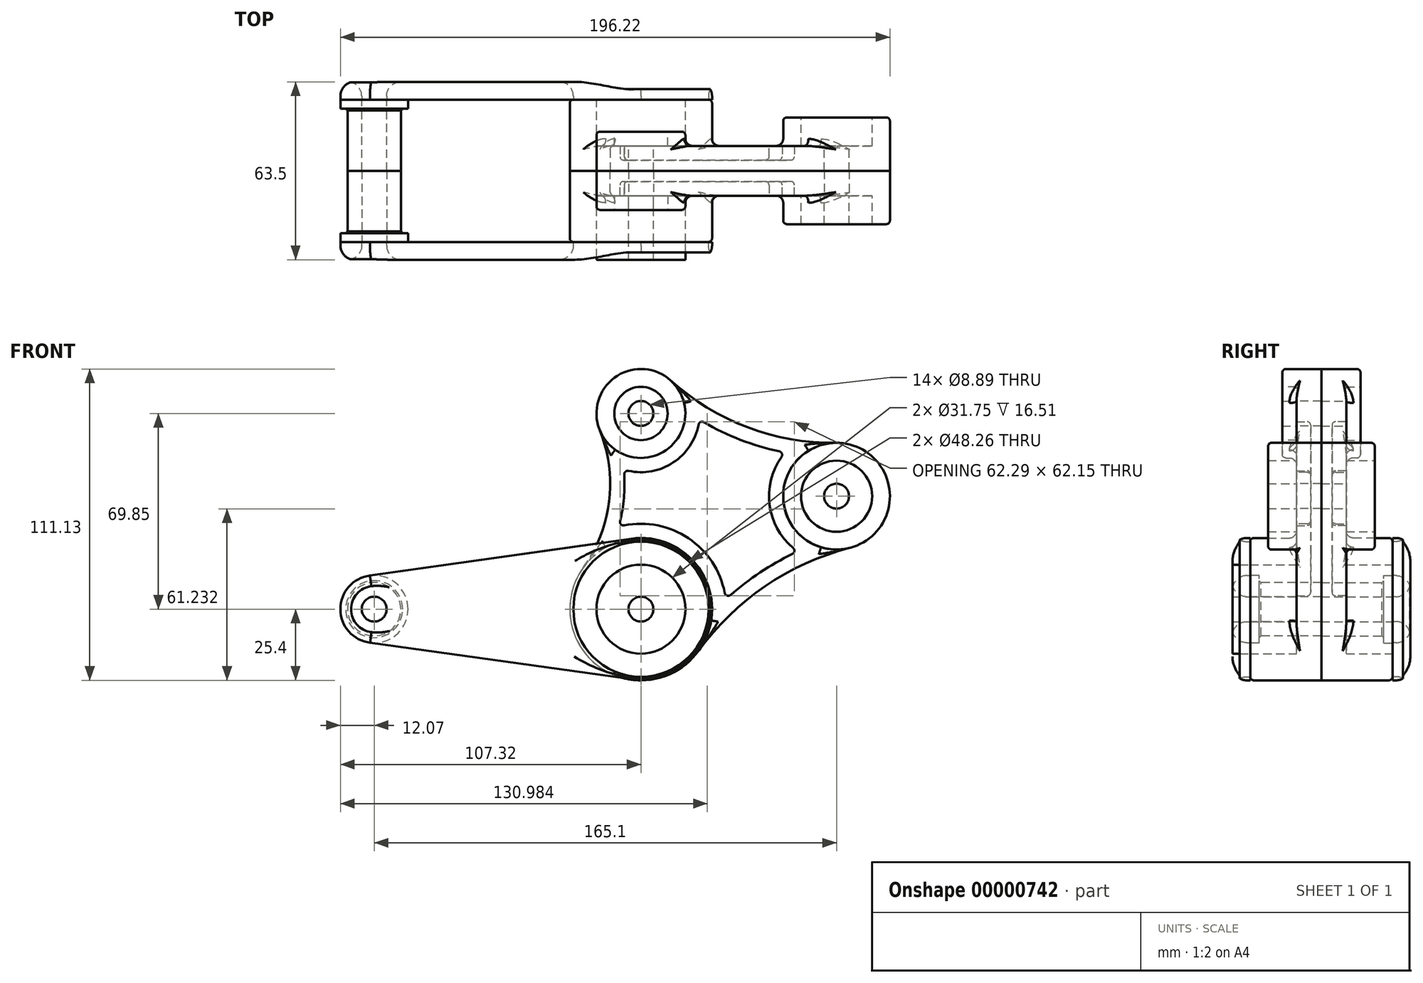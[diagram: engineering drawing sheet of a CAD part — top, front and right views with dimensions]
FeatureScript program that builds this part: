
annotation { "Feature Type Name" : "Feature", "Feature Type Description" : "" }
export const myFeature = defineFeature(function(context is Context, id is Id, definition is map)
    precondition{}
    {
        {
            var Q0;
            Q0=qCreatedBy(makeId("Front.planeOp"),FACE);
            var sketch = newSketch(context, id + "F0", { "sketchPlane" : qUnion([Q0])});
            skCircle(sketch, "E0", {"center": v(0, 0) * mm, "radius": 25.4 * mm});
            skCircle(sketch, "E1", {"center": v(0, 69.85) * mm, "radius": 15.88 * mm});
            skCircle(sketch, "E2", {"center": v(69.85, 40.33) * mm, "radius": 19.05 * mm});
            skLineSegment(sketch, "E3", {"start": v(0, 0) * mm, "end": v(69.85, 40.33) * mm, "construction": true});
            skLineSegment(sketch, "E4", {"start": v(0, 0) * mm, "end": v(74.27, 0) * mm, "construction": true});
            skArc(sketch, "E5", {"start": v(-20.58, 14.89) * mm, "mid": v(-11.3, 38.61) * mm, "end": v(-14.7, 63.85) * mm});
            skArc(sketch, "E6", {"start": v(74.6, 21.88) * mm, "mid": v(44.37, 8.2) * mm, "end": v(20.56, -14.91) * mm});
            skArc(sketch, "E7", {"start": v(10.64, 81.63) * mm, "mid": v(38.02, 64.93) * mm, "end": v(69.6, 59.38) * mm});
            skSolve(sketch);
        }
        {
            var Q0;
            {var subQ0=sQuery(id+"F0.wireOp",EDGE,"E0");var subQ1=sQuery(id+"F0.wireOp",EDGE,"E6");var subQ3=sQuery(id+"F0.wireOp",EDGE,"E5");var subQ4=makeQuery(id+"F0.imprint","INTERSECT",VERTEX,{"derivedFrom":[subQ0,subQ3]});var subQ6=sQuery(id+"F0.wireOp",EDGE,"E1");var subQ9=makeQuery(id+"F0.imprint","INTERSECT",VERTEX,{"derivedFrom":[subQ6,subQ3]});var subQ11=sQuery(id+"F0.wireOp",EDGE,"E2");var subQ13=makeQuery(id+"F0.imprint","INTERSECT",VERTEX,{"derivedFrom":[subQ11,subQ1]});var subQ14=makeQuery(id+"F0.imprint","IMPRINT",EDGE,{"disambiguationData":[TD([[subQ13,1.0]])],"derivedFrom":subQ11});Q0=qUnion([makeQuery(id+"F0.imprint","IMPRINT",FACE,{"disambiguationData":[TD([[makeQuery(id+"F0.imprint","IMPRINT",EDGE,{"disambiguationData":[TD([[subQ4,-1.0]])],"derivedFrom":subQ0}),1.0]])]}),makeQuery(id+"F0.imprint","IMPRINT",FACE,{"disambiguationData":[TD([[makeQuery(id+"F0.imprint","IMPRINT",EDGE,{"disambiguationData":[TD([[subQ9,1.0]])],"derivedFrom":subQ6}),1.0]])]}),makeQuery(id+"F0.imprint","IMPRINT",FACE,{"disambiguationData":[TD([[subQ14,1.0]])]}),makeQuery(id+"F0.imprint","IMPRINT",FACE,{"disambiguationData":[TD([[makeQuery(id+"F0.imprint","IMPRINT",EDGE,{"derivedFrom":subQ3}),-1.0]])]})]);}
            extrude(context, id + "F1", {"entities" : qUnion([Q0]), "depth" : 8.9 * mm});
        }
        {
            var Q0;
            {var subQ0=sQuery(id+"F0.wireOp",EDGE,"E1");var subQ2=makeQuery(id+"F0.imprint","INTERSECT",VERTEX,{"derivedFrom":[subQ0,sQuery(id+"F0.wireOp",EDGE,"E5")]});Q0=makeQuery(id+"F0.imprint","IMPRINT",FACE,{"disambiguationData":[TD([[makeQuery(id+"F0.imprint","IMPRINT",EDGE,{"disambiguationData":[TD([[subQ2,1.0]])],"derivedFrom":subQ0}),1.0]])]});}
            extrude(context, id + "F2", {"entities" : qUnion([Q0]), "operationType" : NewBodyOperationType.ADD, "depth" : 13.97 * mm});
        }
        {
            var Q0;
            {var subQ0=sQuery(id+"F0.wireOp",EDGE,"E2");var subQ2=makeQuery(id+"F0.imprint","INTERSECT",VERTEX,{"derivedFrom":[subQ0,sQuery(id+"F0.wireOp",EDGE,"E6")]});Q0=makeQuery(id+"F0.imprint","IMPRINT",FACE,{"disambiguationData":[TD([[makeQuery(id+"F0.imprint","IMPRINT",EDGE,{"disambiguationData":[TD([[subQ2,1.0]])],"derivedFrom":subQ0}),1.0]])]});}
            extrude(context, id + "F3", {"entities" : qUnion([Q0]), "operationType" : NewBodyOperationType.ADD, "depth" : 19.05 * mm});
        }
        {
            var Q0;
            {var subQ0=sQuery(id+"F0.wireOp",EDGE,"E0");var subQ2=makeQuery(id+"F0.imprint","INTERSECT",VERTEX,{"derivedFrom":[subQ0,sQuery(id+"F0.wireOp",EDGE,"E5")]});Q0=makeQuery(id+"F0.imprint","IMPRINT",FACE,{"disambiguationData":[TD([[makeQuery(id+"F0.imprint","IMPRINT",EDGE,{"disambiguationData":[TD([[subQ2,-1.0]])],"derivedFrom":subQ0}),1.0]])]});}
            extrude(context, id + "F4", {"entities" : qUnion([Q0]), "operationType" : NewBodyOperationType.ADD, "depth" : 25.4 * mm});
        }
        {
            var Q0;
            Q0=makeQuery(id+"F1.opExtrude","CAP_FACE",FACE,{"disambiguationData":[OSD([sQuery(id+"F0.wireOp",EDGE,"E0"),sQuery(id+"F0.wireOp",EDGE,"E1"),sQuery(id+"F0.wireOp",EDGE,"E2"),sQuery(id+"F0.wireOp",EDGE,"E5"),sQuery(id+"F0.wireOp",EDGE,"E6"),sQuery(id+"F0.wireOp",EDGE,"E7")])],"isStart":false});
            var sketch = newSketch(context, id + "F5", { "sketchPlane" : qUnion([Q0])});
            skCircle(sketch, "E8.0", {"center": v(0, 69.85) * mm, "radius": 20.96 * mm});
            skCircle(sketch, "E9.0", {"center": v(69.85, 40.33) * mm, "radius": 24.13 * mm});
            skCircle(sketch, "E10.0", {"center": v(0, 0) * mm, "radius": 30.48 * mm});
            skArc(sketch, "E11.0", {"start": v(-16.46, 11.91) * mm, "mid": v(-6.25, 38) * mm, "end": v(-10, 65.77) * mm});
            skArc(sketch, "E12.0", {"start": v(7.23, 77.86) * mm, "mid": v(36.23, 60.18) * mm, "end": v(69.67, 54.3) * mm});
            skArc(sketch, "E13.0", {"start": v(73.34, 26.8) * mm, "mid": v(41.51, 12.4) * mm, "end": v(16.45, -11.93) * mm});
            skSolve(sketch);
        }
        {
            var Q0;
            {var subQ5=sQuery(id+"F5.wireOp",EDGE,"E12.0");var subQ7=sQuery(id+"F5.wireOp",EDGE,"E8.0");var subQ8=makeQuery(id+"F5.imprint","INTERSECT",VERTEX,{"derivedFrom":[subQ7,subQ5]});Q0=makeQuery(id+"F5.imprint","IMPRINT",FACE,{"disambiguationData":[TD([[makeQuery(id+"F5.imprint","IMPRINT",EDGE,{"disambiguationData":[TD([[subQ8,1.0]])],"derivedFrom":subQ7}),-1.0]])]});}
            extrude(context, id + "F6", {"entities" : qUnion([Q0]), "operationType" : NewBodyOperationType.REMOVE, "oppositeDirection" : true, "depth" : 5.08 * mm});
        }
        {
            var Q0;
            Q0=makeQuery(id+"F4.opExtrude","CAP_FACE",FACE,{"disambiguationData":[OSD([sQuery(id+"F0.wireOp",EDGE,"E0")])],"isStart":false});
            var sketch = newSketch(context, id + "F7", { "sketchPlane" : qUnion([Q0])});
            skCircle(sketch, "E14", {"center": v(0, 0) * mm, "radius": 15.88 * mm});
            skCircle(sketch, "E15.0", {"center": v(0, 69.85) * mm, "radius": 15.88 * mm, "construction": true});
            skCircle(sketch, "E15.1", {"center": v(69.85, 40.33) * mm, "radius": 19.05 * mm, "construction": true});
            skCircle(sketch, "E16", {"center": v(0, 69.85) * mm, "radius": 9.53 * mm});
            skCircle(sketch, "E17", {"center": v(69.85, 40.33) * mm, "radius": 12.7 * mm});
            skSolve(sketch);
        }
        {
            var Q0;
            Q0=makeQuery(id+"F7.imprint","IMPRINT",FACE,{"disambiguationData":[TD([[makeQuery(id+"F7.imprint","IMPRINT",EDGE,{"derivedFrom":sQuery(id+"F7.wireOp",EDGE,"E14")}),1.0]])]});
            var Q1;
            Q1=makeQuery(id+"F7.imprint","IMPRINT",FACE,{"disambiguationData":[TD([[makeQuery(id+"F7.imprint","IMPRINT",EDGE,{"derivedFrom":sQuery(id+"F7.wireOp",EDGE,"E16")}),1.0]])]});
            var Q2;
            Q2=makeQuery(id+"F7.imprint","IMPRINT",FACE,{"disambiguationData":[TD([[makeQuery(id+"F7.imprint","IMPRINT",EDGE,{"derivedFrom":sQuery(id+"F7.wireOp",EDGE,"E17")}),1.0]])]});
            var Q3;
            Q3=makeQuery(id+"F1.opExtrude","CAP_FACE",FACE,{"disambiguationData":[OSD([sQuery(id+"F0.wireOp",EDGE,"E0"),sQuery(id+"F0.wireOp",EDGE,"E1"),sQuery(id+"F0.wireOp",EDGE,"E2"),sQuery(id+"F0.wireOp",EDGE,"E5"),sQuery(id+"F0.wireOp",EDGE,"E6"),sQuery(id+"F0.wireOp",EDGE,"E7")])],"isStart":false});
            extrude(context, id + "F8", {"entities" : qUnion([Q0, Q1, Q2]), "operationType" : NewBodyOperationType.REMOVE, "endBound" : BoundingType.UP_TO_SURFACE, "oppositeDirection" : true, "endBoundEntityFace" : qUnion([Q3]), "depth" : 25.4 * mm});
        }
        {
            var Q0;
            Q0=makeQuery(id+"F8.boolean.opBoolean","COPY",FACE,{"derivedFrom":makeQuery(id+"F8.opExtrude","CAP_FACE",FACE,{"disambiguationData":[OSD([sQuery(id+"F7.wireOp",EDGE,"E17")])],"isStart":false})});
            var sketch = newSketch(context, id + "F9", { "sketchPlane" : qUnion([Q0])});
            skCircle(sketch, "E18.0", {"center": v(0, 69.85) * mm, "radius": 9.53 * mm});
            skCircle(sketch, "E18.1", {"center": v(0, 0) * mm, "radius": 15.88 * mm});
            skCircle(sketch, "E18.2", {"center": v(69.85, 40.33) * mm, "radius": 12.7 * mm});
            skCircle(sketch, "E19", {"center": v(0, 0) * mm, "radius": 4.45 * mm});
            skCircle(sketch, "E20", {"center": v(0, 69.85) * mm, "radius": 4.45 * mm});
            skCircle(sketch, "E21", {"center": v(69.85, 40.33) * mm, "radius": 4.45 * mm});
            skSolve(sketch);
        }
        {
            var Q0;
            Q0=makeQuery(id+"F9.imprint","IMPRINT",FACE,{"disambiguationData":[TD([[makeQuery(id+"F9.imprint","IMPRINT",EDGE,{"derivedFrom":sQuery(id+"F9.wireOp",EDGE,"E20")}),1.0]])]});
            var Q1;
            Q1=makeQuery(id+"F9.imprint","IMPRINT",FACE,{"disambiguationData":[TD([[makeQuery(id+"F9.imprint","IMPRINT",EDGE,{"derivedFrom":sQuery(id+"F9.wireOp",EDGE,"E21")}),1.0]])]});
            var Q2;
            Q2=makeQuery(id+"F9.imprint","IMPRINT",FACE,{"disambiguationData":[TD([[makeQuery(id+"F9.imprint","IMPRINT",EDGE,{"derivedFrom":sQuery(id+"F9.wireOp",EDGE,"E19")}),1.0]])]});
            extrude(context, id + "F10", {"entities" : qUnion([Q0, Q1, Q2]), "operationType" : NewBodyOperationType.REMOVE, "endBound" : BoundingType.THROUGH_ALL, "oppositeDirection" : true, "depth" : 25.4 * mm});
        }
        {
            var Q0;
            Q0=makeQuery(id+"F6.boolean.opBoolean","COPY",FACE,{"derivedFrom":makeQuery(id+"F6.opExtrude","CAP_FACE",FACE,{"disambiguationData":[OSD([sQuery(id+"F5.wireOp",EDGE,"E8.0"),sQuery(id+"F5.wireOp",EDGE,"E9.0"),sQuery(id+"F5.wireOp",EDGE,"E10.0"),sQuery(id+"F5.wireOp",EDGE,"E11.0"),sQuery(id+"F5.wireOp",EDGE,"E12.0"),sQuery(id+"F5.wireOp",EDGE,"E13.0")])],"isStart":false})});
            var Q1;
            Q1=makeQuery(id+"F6.boolean.opBoolean","COPY",EDGE,{"derivedFrom":makeQuery(id+"F6.opExtrude","SWEPT_EDGE",EDGE,{"disambiguationData":[OSD([sQuery(id+"F5.wireOp",EDGE,"E8.0"),sQuery(id+"F5.wireOp",EDGE,"E11.0")])]})});
            var Q2;
            Q2=makeQuery(id+"F6.boolean.opBoolean","COPY",EDGE,{"derivedFrom":makeQuery(id+"F6.opExtrude","SWEPT_EDGE",EDGE,{"disambiguationData":[OSD([sQuery(id+"F5.wireOp",EDGE,"E8.0"),sQuery(id+"F5.wireOp",EDGE,"E12.0")])]})});
            var Q3;
            Q3=makeQuery(id+"F6.boolean.opBoolean","COPY",EDGE,{"derivedFrom":makeQuery(id+"F6.opExtrude","SWEPT_EDGE",EDGE,{"disambiguationData":[OSD([sQuery(id+"F5.wireOp",EDGE,"E9.0"),sQuery(id+"F5.wireOp",EDGE,"E12.0")])]})});
            var Q4;
            Q4=makeQuery(id+"F6.boolean.opBoolean","COPY",EDGE,{"derivedFrom":makeQuery(id+"F6.opExtrude","SWEPT_EDGE",EDGE,{"disambiguationData":[OSD([sQuery(id+"F5.wireOp",EDGE,"E9.0"),sQuery(id+"F5.wireOp",EDGE,"E13.0")])]})});
            var Q5;
            Q5=makeQuery(id+"F6.boolean.opBoolean","COPY",EDGE,{"derivedFrom":makeQuery(id+"F6.opExtrude","SWEPT_EDGE",EDGE,{"disambiguationData":[OSD([sQuery(id+"F5.wireOp",EDGE,"E10.0"),sQuery(id+"F5.wireOp",EDGE,"E13.0")])]})});
            var Q6;
            Q6=makeQuery(id+"F6.boolean.opBoolean","COPY",EDGE,{"derivedFrom":makeQuery(id+"F6.opExtrude","SWEPT_EDGE",EDGE,{"disambiguationData":[OSD([sQuery(id+"F5.wireOp",EDGE,"E10.0"),sQuery(id+"F5.wireOp",EDGE,"E11.0")])]})});
            var Q7;
            Q7=makeQuery(id+"F6.boolean.opBoolean","COPY",EDGE,{"derivedFrom":makeQuery(id+"F6.opExtrude","CAP_EDGE",EDGE,{"disambiguationData":[OSD([sQuery(id+"F5.wireOp",EDGE,"E10.0")])],"isStart":true})});
            var Q8;
            Q8=makeQuery(id+"F1.opExtrude","CAP_EDGE",EDGE,{"disambiguationData":[OSD([sQuery(id+"F0.wireOp",EDGE,"E7")])],"isStart":false});
            var Q9;
            Q9=makeQuery(id+"F1.opExtrude","CAP_EDGE",EDGE,{"disambiguationData":[OSD([sQuery(id+"F0.wireOp",EDGE,"E6")])],"isStart":false});
            var Q10;
            Q10=makeQuery(id+"F1.opExtrude","CAP_EDGE",EDGE,{"disambiguationData":[OSD([sQuery(id+"F0.wireOp",EDGE,"E5")])],"isStart":false});
            var Q11;
            Q11=makeQuery(id+"F4.opExtrude","CAP_EDGE",EDGE,{"disambiguationData":[OSD([sQuery(id+"F0.wireOp",EDGE,"E0")])],"isStart":false});
            var Q12;
            Q12=makeQuery(id+"F3.opExtrude","CAP_EDGE",EDGE,{"disambiguationData":[OSD([sQuery(id+"F0.wireOp",EDGE,"E2")])],"isStart":false});
            var Q13;
            Q13=makeQuery(id+"F2.opExtrude","CAP_EDGE",EDGE,{"disambiguationData":[OSD([sQuery(id+"F0.wireOp",EDGE,"E1")])],"isStart":false});
            fillet(context, id + "F11", {"entities" : qUnion([Q0, Q1, Q2, Q3, Q4, Q5, Q6, Q7, Q8, Q9, Q10, Q11, Q12, Q13]), "radius" : 1.27 * mm, "tangentPropagation" : true, "allowEdgeOverflow" : false});
        }
        {
            var Q0;
            {var subQ0=sQuery(id+"F0.wireOp",EDGE,"E2");Q0=makeQuery(id+"F3.boolean.opBoolean","INTERSECT",EDGE,{"derivedFrom":[makeQuery(id+"F1.opExtrude","CAP_FACE",FACE,{"disambiguationData":[OSD([sQuery(id+"F0.wireOp",EDGE,"E0"),sQuery(id+"F0.wireOp",EDGE,"E1"),subQ0,sQuery(id+"F0.wireOp",EDGE,"E5"),sQuery(id+"F0.wireOp",EDGE,"E6"),sQuery(id+"F0.wireOp",EDGE,"E7")])],"isStart":false}),makeQuery(id+"F3.opExtrude","SWEPT_FACE",FACE,{"disambiguationData":[OSD([subQ0])]})]});}
            var Q1;
            {var subQ0=sQuery(id+"F0.wireOp",EDGE,"E0");Q1=makeQuery(id+"F4.boolean.opBoolean","INTERSECT",EDGE,{"derivedFrom":[makeQuery(id+"F1.opExtrude","CAP_FACE",FACE,{"disambiguationData":[OSD([subQ0,sQuery(id+"F0.wireOp",EDGE,"E1"),sQuery(id+"F0.wireOp",EDGE,"E2"),sQuery(id+"F0.wireOp",EDGE,"E5"),sQuery(id+"F0.wireOp",EDGE,"E6"),sQuery(id+"F0.wireOp",EDGE,"E7")])],"isStart":false}),makeQuery(id+"F4.opExtrude","SWEPT_FACE",FACE,{"disambiguationData":[OSD([subQ0])]})]});}
            var Q2;
            {var subQ0=sQuery(id+"F0.wireOp",EDGE,"E1");Q2=makeQuery(id+"F2.boolean.opBoolean","INTERSECT",EDGE,{"derivedFrom":[makeQuery(id+"F1.opExtrude","CAP_FACE",FACE,{"disambiguationData":[OSD([sQuery(id+"F0.wireOp",EDGE,"E0"),subQ0,sQuery(id+"F0.wireOp",EDGE,"E2"),sQuery(id+"F0.wireOp",EDGE,"E5"),sQuery(id+"F0.wireOp",EDGE,"E6"),sQuery(id+"F0.wireOp",EDGE,"E7")])],"isStart":false}),makeQuery(id+"F2.opExtrude","SWEPT_FACE",FACE,{"disambiguationData":[OSD([subQ0])]})]});}
            fillet(context, id + "F12", {"entities" : qUnion([Q0, Q1, Q2]), "radius" : 2.54 * mm, "tangentPropagation" : true, "allowEdgeOverflow" : false});
        }
        {
            var Q0;
            Q0=makeQuery(id+"F1.opExtrude","SWEPT_BODY",BODY,{"disambiguationData":[OSD([sQuery(id+"F0.wireOp",EDGE,"E0"),sQuery(id+"F0.wireOp",EDGE,"E1"),sQuery(id+"F0.wireOp",EDGE,"E2"),sQuery(id+"F0.wireOp",EDGE,"E5"),sQuery(id+"F0.wireOp",EDGE,"E6"),sQuery(id+"F0.wireOp",EDGE,"E7")])]});
            var Q1;
            Q1=qCreatedBy(makeId("Front.planeOp"),FACE);
            mirror(context, id + "F13", {"entities" : qUnion([Q0]), "mirrorPlane" : qUnion([Q1])});
        }
        {
            var Q0;
            Q0=makeQuery(id+"F8.boolean.opBoolean","COPY",FACE,{"derivedFrom":makeQuery(id+"F8.opExtrude","CAP_FACE",FACE,{"disambiguationData":[OSD([sQuery(id+"F7.wireOp",EDGE,"E16")])],"isStart":false})});
            var sketch = newSketch(context, id + "F14", { "sketchPlane" : qUnion([Q0])});
            skCircle(sketch, "E22.0.0", {"center": v(0, 69.85) * mm, "radius": 9.53 * mm});
            skSolve(sketch);
        }
        {
            var Q0;
            Q0=makeQuery(id+"F14.imprint","IMPRINT",FACE,{"disambiguationData":[TD([[makeQuery(id+"F14.imprint","IMPRINT",EDGE,{"derivedFrom":sQuery(id+"F14.wireOp",EDGE,"E22.0.0")}),-1.0]])]});
            var Q1;
            Q1=makeQuery(id+"F2.opExtrude","CAP_FACE",FACE,{"disambiguationData":[OSD([sQuery(id+"F0.wireOp",EDGE,"E1")])],"isStart":false});
            extrude(context, id + "F15", {"entities" : qUnion([Q0]), "endBound" : BoundingType.UP_TO_SURFACE, "endBoundEntityFace" : qUnion([Q1]), "depth" : 25.4 * mm});
        }
        {
            var Q0;
            Q0=makeQuery(id+"F8.boolean.opBoolean","COPY",FACE,{"derivedFrom":makeQuery(id+"F8.opExtrude","CAP_FACE",FACE,{"disambiguationData":[OSD([sQuery(id+"F7.wireOp",EDGE,"E17")])],"isStart":false})});
            var Q1;
            Q1=makeQuery(id+"F3.opExtrude","CAP_FACE",FACE,{"disambiguationData":[OSD([sQuery(id+"F0.wireOp",EDGE,"E2")])],"isStart":false});
            extrude(context, id + "F16", {"entities" : qUnion([Q0]), "endBound" : BoundingType.UP_TO_SURFACE, "endBoundEntityFace" : qUnion([Q1]), "depth" : 25.4 * mm});
        }
        {
            var Q0;
            Q0=makeQuery(id+"F8.boolean.opBoolean","COPY",FACE,{"derivedFrom":makeQuery(id+"F8.opExtrude","CAP_FACE",FACE,{"disambiguationData":[OSD([sQuery(id+"F7.wireOp",EDGE,"E14")])],"isStart":false})});
            var sketch = newSketch(context, id + "F17", { "sketchPlane" : qUnion([Q0])});
            skCircle(sketch, "E23.0", {"center": v(0, 0) * mm, "radius": 4.45 * mm});
            skCircle(sketch, "E23.1", {"center": v(0, 0) * mm, "radius": 15.88 * mm});
            skSolve(sketch);
        }
        {
            var Q0;
            Q0=makeQuery(id+"F17.imprint","IMPRINT",FACE,{"disambiguationData":[TD([[makeQuery(id+"F17.imprint","IMPRINT",EDGE,{"derivedFrom":sQuery(id+"F17.wireOp",EDGE,"E23.0")}),-1.0]])]});
            var Q1;
            Q1=makeQuery(id+"F4.opExtrude","CAP_FACE",FACE,{"disambiguationData":[OSD([sQuery(id+"F0.wireOp",EDGE,"E0")])],"isStart":false});
            extrude(context, id + "F18", {"entities" : qUnion([Q0]), "endBound" : BoundingType.UP_TO_SURFACE, "endBoundEntityFace" : qUnion([Q1]), "depth" : 25.4 * mm});
        }
        {
            var Q0;
            Q0=qCreatedBy(makeId("Top.planeOp"),FACE);
            var sketch = newSketch(context, id + "F19", { "sketchPlane" : qUnion([Q0])});
            skLineSegment(sketch, "E24", {"start": v(-90.8, 0) * mm, "end": v(-90.8, -25.4) * mm});
            skLineSegment(sketch, "E25", {"start": v(-90.8, -25.4) * mm, "end": v(-83.19, -25.4) * mm});
            skLineSegment(sketch, "E26", {"start": v(-83.19, -25.4) * mm, "end": v(-83.19, -22.23) * mm});
            skLineSegment(sketch, "E27", {"start": v(-83.19, -22.23) * mm, "end": v(-85.1, -22.23) * mm});
            skLineSegment(sketch, "E28", {"start": v(-85.1, -22.23) * mm, "end": v(-85.73, -21.6) * mm});
            skLineSegment(sketch, "E29", {"start": v(-85.73, -21.6) * mm, "end": v(-85.73, 0) * mm});
            skLineSegment(sketch, "E30", {"start": v(-85.73, 0) * mm, "end": v(-90.8, 0) * mm});
            skLineSegment(sketch, "E31.0", {"start": v(24.13, -25.4) * mm, "end": v(-24.13, -25.4) * mm});
            skLineSegment(sketch, "E32", {"start": v(-95.25, -25.4) * mm, "end": v(-95.25, 0) * mm, "construction": true});
            skSolve(sketch);
        }
        {
            var Q0;
            Q0=makeQuery(id+"F19.imprint","IMPRINT",FACE,{"disambiguationData":[TD([[makeQuery(id+"F19.imprint","IMPRINT",EDGE,{"derivedFrom":sQuery(id+"F19.wireOp",EDGE,"E24")}),1.0]])]});
            var Q1;
            Q1=sQuery(id+"F19.wireOp",EDGE,"E32");
            revolve(context, id + "F20", {"entities" : qUnion([Q0]), "axis" : qUnion([Q1]), "revolveType" : RevolveType.FULL});
        }
        {
            var Q0;
            Q0=makeQuery(id+"F20.opRevolve","SWEPT_BODY",BODY,{"disambiguationData":[OSD([sQuery(id+"F19.wireOp",EDGE,"E24"),sQuery(id+"F19.wireOp",EDGE,"E25"),sQuery(id+"F19.wireOp",EDGE,"E26"),sQuery(id+"F19.wireOp",EDGE,"E27"),sQuery(id+"F19.wireOp",EDGE,"E28"),sQuery(id+"F19.wireOp",EDGE,"E29"),sQuery(id+"F19.wireOp",EDGE,"E30")])]});
            var Q1;
            Q1=makeQuery(id+"F20.opRevolve","SWEPT_FACE",FACE,{"disambiguationData":[OSD([sQuery(id+"F19.wireOp",EDGE,"E30")])]});
            mirror(context, id + "F21", {"entities" : qUnion([Q0]), "mirrorPlane" : qUnion([Q1])});
        }
        {
            var Q0;
            Q0=makeQuery(id+"F4.opExtrude","CAP_FACE",FACE,{"disambiguationData":[OSD([sQuery(id+"F0.wireOp",EDGE,"E0")])],"isStart":false});
            var sketch = newSketch(context, id + "F22", { "sketchPlane" : qUnion([Q0])});
            skCircle(sketch, "E33.0", {"center": v(-95.25, 0) * mm, "radius": 12.07 * mm});
            skArc(sketch, "E34.0", {"start": v(-96.74, 11.97) * mm, "mid": v(-107.31, -0.03) * mm, "end": v(-96.7, -11.98) * mm});
            skCircle(sketch, "E34.1", {"center": v(-95.25, 0) * mm, "radius": 4.45 * mm});
            skCircle(sketch, "E35.2", {"center": v(0, 0) * mm, "radius": 25.4 * mm});
            skArc(sketch, "E36.2", {"start": v(-6.92, -24.44) * mm, "mid": v(25.34, -1.72) * mm, "end": v(-3.56, 25.15) * mm});
            skCircle(sketch, "E36.3", {"center": v(0, 0) * mm, "radius": 4.45 * mm});
            skLineSegment(sketch, "E37", {"start": v(-96.74, 11.97) * mm, "end": v(-3.56, 25.15) * mm});
            skLineSegment(sketch, "E38", {"start": v(-96.7, -11.98) * mm, "end": v(0, -25.4) * mm});
            skSolve(sketch);
        }
        {
            var Q0;
            {var subQ0=sQuery(id+"F0.wireOp",EDGE,"E0");Q0=makeQuery(id+"F22.imprint","IMPRINT",FACE,{"disambiguationData":[TD([[makeQuery(id+"F22.imprint","IMPRINT",EDGE,{"derivedFrom":makeQuery(id+"F11.opFillet","BLEND_EDGE",EDGE,{"blendedFrom":[makeQuery(id+"F4.opExtrude","CAP_EDGE",EDGE,{"disambiguationData":[OSD([subQ0])],"isStart":false}),makeQuery(id+"F4.opExtrude","CAP_FACE",FACE,{"disambiguationData":[OSD([subQ0])],"isStart":false})],"blendedInto":[makeQuery(id+"F4.opExtrude","CAP_FACE",FACE,{"disambiguationData":[OSD([subQ0])],"isStart":false})]})}),-1.0]])]});}
            var Q1;
            {var subQ0=sQuery(id+"F22.wireOp",EDGE,"E38");var subQ1=sQuery(id+"F22.wireOp",EDGE,"E35.2");var subQ3=makeQuery(id+"F22.imprint","INTERSECT",VERTEX,{"disambiguationData":[OD(0.0)],"derivedFrom":[subQ1,subQ0]});Q1=makeQuery(id+"F22.imprint","IMPRINT",FACE,{"disambiguationData":[TD([[makeQuery(id+"F22.imprint","IMPRINT",EDGE,{"disambiguationData":[TD([[subQ3,1.0]])],"derivedFrom":subQ1}),1.0]])]});}
            var Q2;
            Q2=makeQuery(id+"F22.imprint","IMPRINT",FACE,{"disambiguationData":[TD([[makeQuery(id+"F22.imprint","IMPRINT",EDGE,{"derivedFrom":sQuery(id+"F22.wireOp",EDGE,"E34.1")}),-1.0]])]});
            var Q3;
            {var subQ5=sQuery(id+"F22.wireOp",EDGE,"E37");Q3=makeQuery(id+"F22.imprint","IMPRINT",FACE,{"disambiguationData":[TD([[makeQuery(id+"F22.imprint","IMPRINT",EDGE,{"derivedFrom":subQ5}),-1.0]])]});}
            var Q4;
            Q4=makeQuery(id+"F22.imprint","IMPRINT",FACE,{"disambiguationData":[TD([[makeQuery(id+"F22.imprint","IMPRINT",EDGE,{"derivedFrom":makeQuery(id+"F8.boolean.opBoolean","COPY",EDGE,{"derivedFrom":makeQuery(id+"F8.opExtrude","CAP_EDGE",EDGE,{"disambiguationData":[OSD([sQuery(id+"F7.wireOp",EDGE,"E14")])],"isStart":true})})}),-1.0]])]});
            var Q5;
            Q5=makeQuery(id+"F22.imprint","IMPRINT",FACE,{"disambiguationData":[TD([[makeQuery(id+"F22.imprint","IMPRINT",EDGE,{"derivedFrom":sQuery(id+"F22.wireOp",EDGE,"E36.3")}),-1.0]])]});
            extrude(context, id + "F23", {"entities" : qUnion([Q0, Q1, Q2, Q3, Q4, Q5]), "depth" : 6.35 * mm});
        }
        {
            var Q0;
            Q0=makeQuery(id+"F23.opExtrude","CAP_FACE",FACE,{"disambiguationData":[OSD([sQuery(id+"F22.wireOp",EDGE,"E35.2"),sQuery(id+"F22.wireOp",EDGE,"E33.0"),sQuery(id+"F22.wireOp",EDGE,"E34.1"),sQuery(id+"F22.wireOp",EDGE,"E36.3"),sQuery(id+"F22.wireOp",EDGE,"E37"),sQuery(id+"F22.wireOp",EDGE,"E38")])],"isStart":false});
            fillet(context, id + "F24", {"entities" : qUnion([Q0]), "radius" : 5.08 * mm, "tangentPropagation" : true, "allowEdgeOverflow" : false});
        }
        {
            var Q0;
            Q0=makeQuery(id+"F23.opExtrude","SWEPT_BODY",BODY,{"disambiguationData":[OSD([sQuery(id+"F22.wireOp",EDGE,"E35.2"),sQuery(id+"F22.wireOp",EDGE,"E33.0"),sQuery(id+"F22.wireOp",EDGE,"E34.1"),sQuery(id+"F22.wireOp",EDGE,"E36.3"),sQuery(id+"F22.wireOp",EDGE,"E37"),sQuery(id+"F22.wireOp",EDGE,"E38")])]});
            var Q1;
            Q1=qCreatedBy(makeId("Front.planeOp"),FACE);
            mirror(context, id + "F25", {"entities" : qUnion([Q0]), "mirrorPlane" : qUnion([Q1])});
        }
    });
